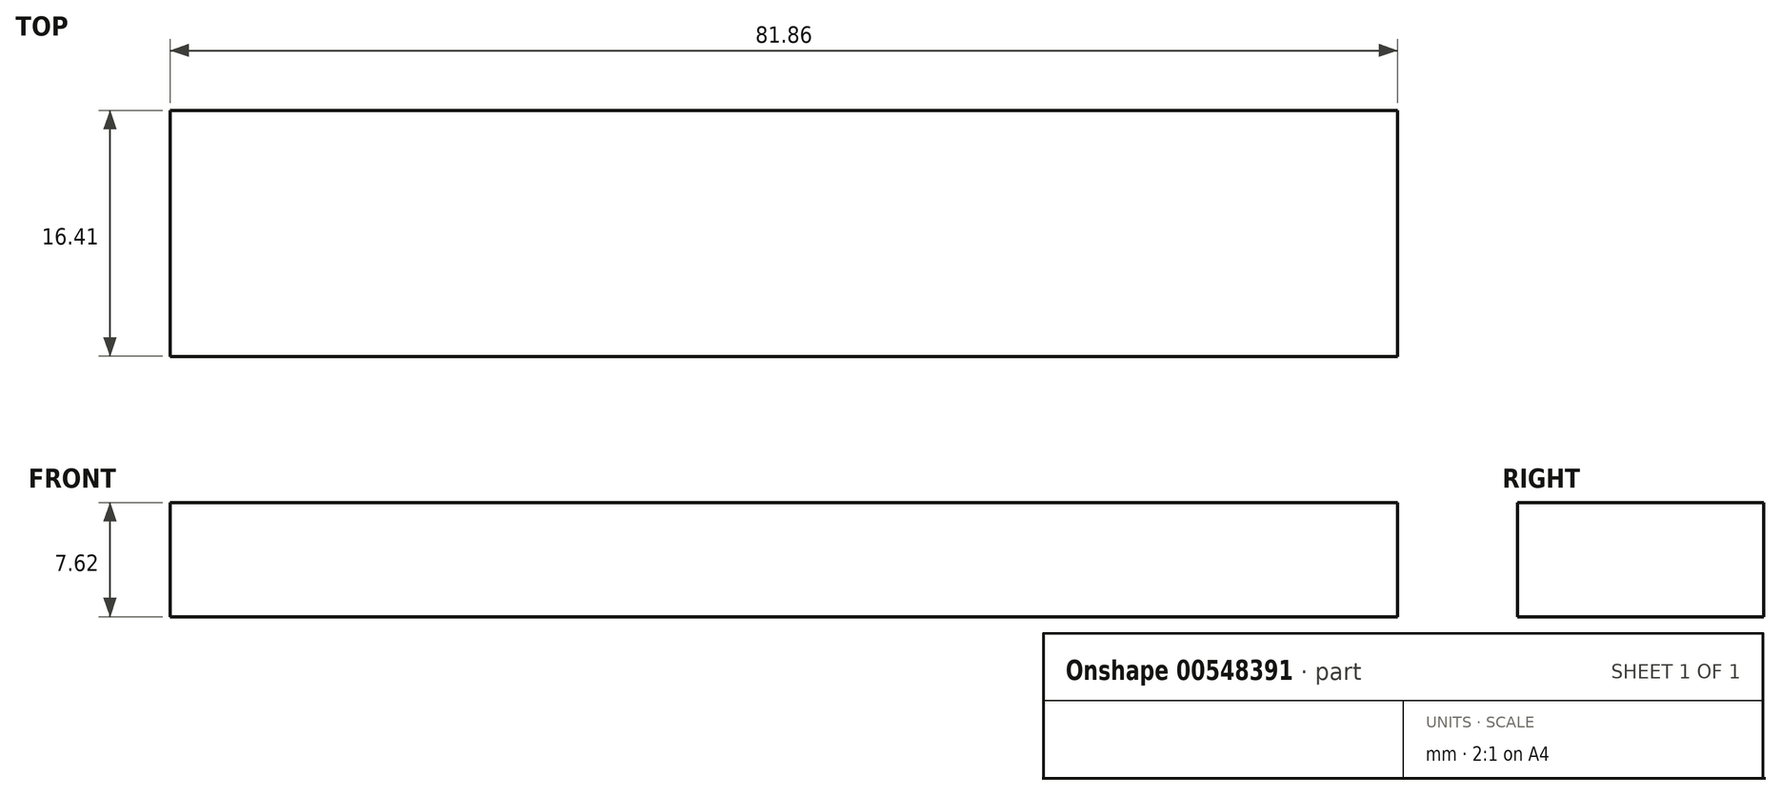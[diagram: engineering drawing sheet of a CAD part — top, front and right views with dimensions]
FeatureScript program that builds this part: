
annotation { "Feature Type Name" : "Feature", "Feature Type Description" : "" }
export const myFeature = defineFeature(function(context is Context, id is Id, definition is map)
    precondition{}
    {
        {
            var Q0;
            Q0=qCreatedBy(makeId("Top.planeOp"),FACE);
            var sketch = newSketch(context, id + "F0", { "sketchPlane" : qUnion([Q0])});
            skLineSegment(sketch, "E0.bottom", {"start": v(-49.38, 6.45) * mm, "end": v(57.88, 6.45) * mm});
            skLineSegment(sketch, "E0.top", {"start": v(-49.38, -9.96) * mm, "end": v(57.88, -9.96) * mm});
            skLineSegment(sketch, "E0.left", {"start": v(-49.38, 6.45) * mm, "end": v(-49.38, -9.96) * mm});
            skLineSegment(sketch, "E0.right", {"start": v(57.88, 6.45) * mm, "end": v(57.88, -9.96) * mm});
            skSolve(sketch);
        }
        {
            var Q0;
            Q0=makeQuery(id+"F0.imprint","IMPRINT",FACE,{"disambiguationData":[TD([[makeQuery(id+"F0.imprint","IMPRINT",EDGE,{"derivedFrom":sQuery(id+"F0.wireOp",EDGE,"E0.bottom")}),-1.0]])]});
            extrude(context, id + "F1", {"entities" : qUnion([Q0]), "depth" : 7.62 * mm, "offsetDistance" : 25.4 * mm});
        }
        {
            var Q0;
            Q0=makeQuery(id+"F1.opExtrude","SWEPT_FACE",FACE,{"disambiguationData":[OSD([sQuery(id+"F0.wireOp",EDGE,"E0.right")])]});
            extrude(context, id + "F2", {"entities" : qUnion([Q0]), "operationType" : NewBodyOperationType.REMOVE, "oppositeDirection" : true, "depth" : 25.4 * mm, "offsetDistance" : 25.4 * mm});
        }
    });
